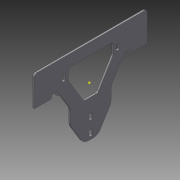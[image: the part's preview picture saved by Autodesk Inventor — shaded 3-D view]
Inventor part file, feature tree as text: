
AUTODESK INVENTOR PART (.ipt)
format: ipt  version: 2015 (Build 190159000, 159)  size: 219,136 bytes
history: native  units: mm
features: extrude x2, fillet x2, sketch x1
ambient origin geometry x8: Origin, YZ Plane, XZ Plane, XY Plane, X Axis, Y Axis, Z Axis, Center Point
bodies: Body1 (feature_tree)
feature tree (5):
  extrude  "Extrusion11"  Depth=200.0mm
  extrude  "Extrusion13"  Depth=10.0mm
  fillet  "Fillet1"  Radius=6.0mm
  fillet  "Fillet2"  Radius=10.0mm
  sketch  "Sketch4"  dims[d8=0.0mm d65=200.0mm d69=20.0mm d71=20.0mm d72=43.5mm d73=43.5mm d74=60.0mm d75=60.0mm d76=10.0mm d77=10.0mm d78=60.0mm d79=90.0mm d80=43.5mm d81=43.5mm d87=15.0mm d115=10.0mm d116=6.0mm d118=10.0mm d119=6.0mm d120=15.0mm d147=65.0mm d173=25.0mm d187=100.0mm d191=30.0mm d192=30.0mm d194=6.000296mm d195=6.0mm d196=10.0mm d197=10.0mm d198=52.999704mm d199=53.0mm d204=150.0mm d210=3.0mm d211=0.0mm d213=20.0mm d214=20.0mm d218=65.0mm d219=40.0mm d220=5.0mm d233=25.922561mm d235=5.0mm d236=20.0mm d237=6.0mm d238=27.0mm d239=10.0mm d240=5.0mm d241=6.0mm d242=10.0mm d243=5.0mm d244=27.0mm d245=10.0mm d246=0.0mm d247=15.0mm d248=5.0mm d249=5.0mm]
